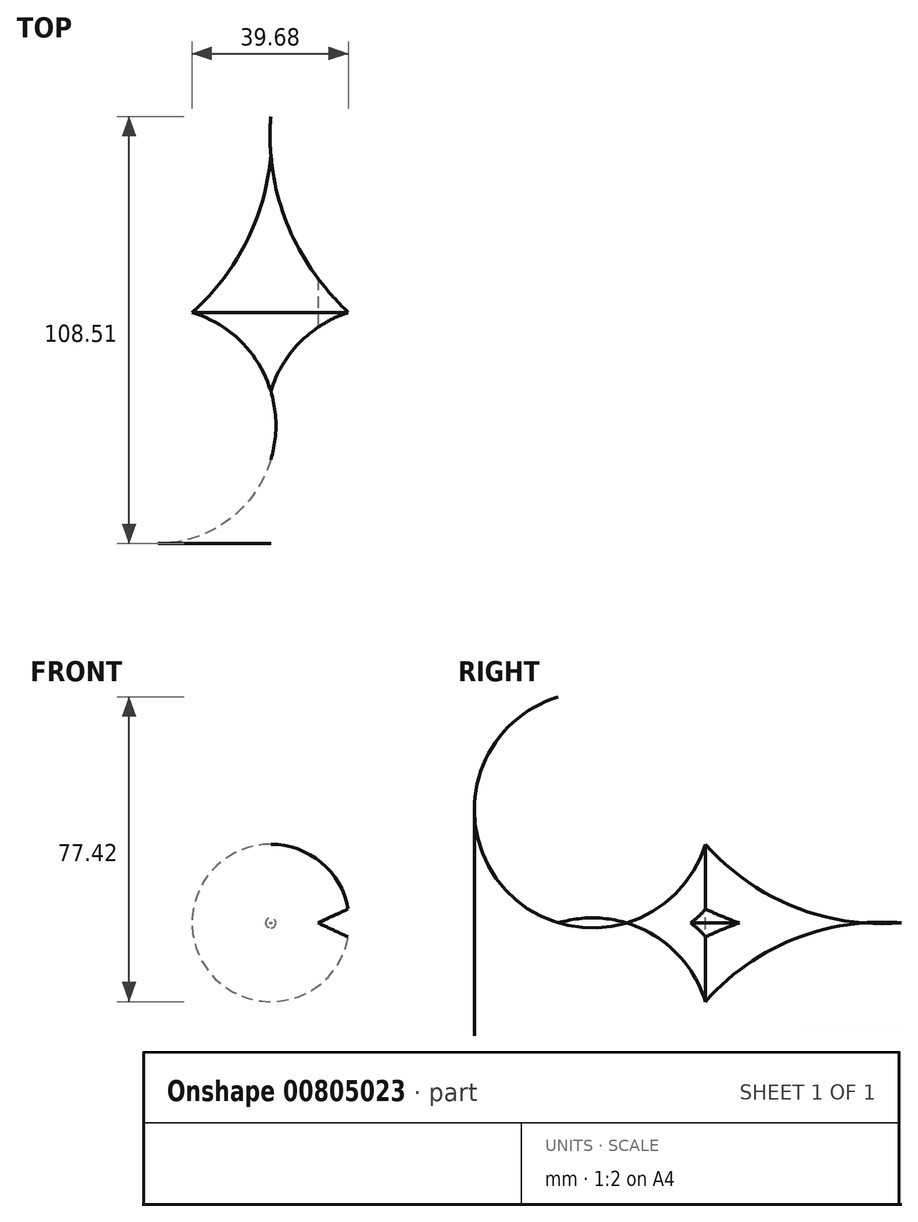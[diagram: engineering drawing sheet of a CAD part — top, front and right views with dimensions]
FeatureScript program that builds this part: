
annotation { "Feature Type Name" : "Feature", "Feature Type Description" : "" }
export const myFeature = defineFeature(function(context is Context, id is Id, definition is map)
    precondition{}
    {
        {
            var Q0;
            Q0=qCreatedBy(makeId("Top.planeOp"),FACE);
            var sketch = newSketch(context, id + "F0", { "sketchPlane" : qUnion([Q0])});
            skLineSegment(sketch, "E0", {"start": v(0, 62.83) * mm, "end": v(0, -53) * mm, "construction": true});
            skArc(sketch, "E1", {"start": v(20, 20) * mm, "mid": v(7.5, 12.5) * mm, "end": v(0, 0) * mm});
            skArc(sketch, "E2", {"start": v(0, 60) * mm, "mid": v(6.13, 38.07) * mm, "end": v(20, 20) * mm});
            skLineSegment(sketch, "E3", {"start": v(0, 60) * mm, "end": v(0, 0) * mm});
            skSolve(sketch);
        }
        {
            var Q0;
            Q0 = qSketchRegion(id + "F0", true);
            var Q1;
            Q1=sQuery(id+"F0.wireOp",EDGE,"E0");
            revolve(context, id + "F1", {"surfaceOperationType" : NewSurfaceOperationType.NEW, "entities" : qUnion([Q0]), "axis" : qUnion([Q1]), "revolveType" : RevolveType.FULL});
        }
        {
            var Q0;
            Q0=qCreatedBy(makeId("Front.planeOp"),FACE);
            var sketch = newSketch(context, id + "F2", { "sketchPlane" : qUnion([Q0])});
            skCircle(sketch, "E4.0", {"center": v(0, 0) * mm, "radius": 20 * mm});
            skLineSegment(sketch, "E5", {"start": v(19.68, 3.58) * mm, "end": v(12, 0) * mm});
            skLineSegment(sketch, "E6", {"start": v(12, 0) * mm, "end": v(19.68, -3.58) * mm});
            skLineSegment(sketch, "E7", {"start": v(0, 0) * mm, "end": v(34.61, 0) * mm, "construction": true});
            skSolve(sketch);
        }
        {
            var Q0;
            {var subQ0=sQuery(id+"F2.wireOp",EDGE,"E5");Q0=makeQuery(id+"F2.imprint","IMPRINT",FACE,{"disambiguationData":[TD([[makeQuery(id+"F2.imprint","IMPRINT",EDGE,{"derivedFrom":subQ0}),1.0]])]});}
            extrude(context, id + "F3", {"entities" : qUnion([Q0]), "operationType" : NewBodyOperationType.REMOVE, "oppositeDirection" : true, "depth" : 32.6 * mm, "offsetDistance" : 25 * mm});
        }
    });
